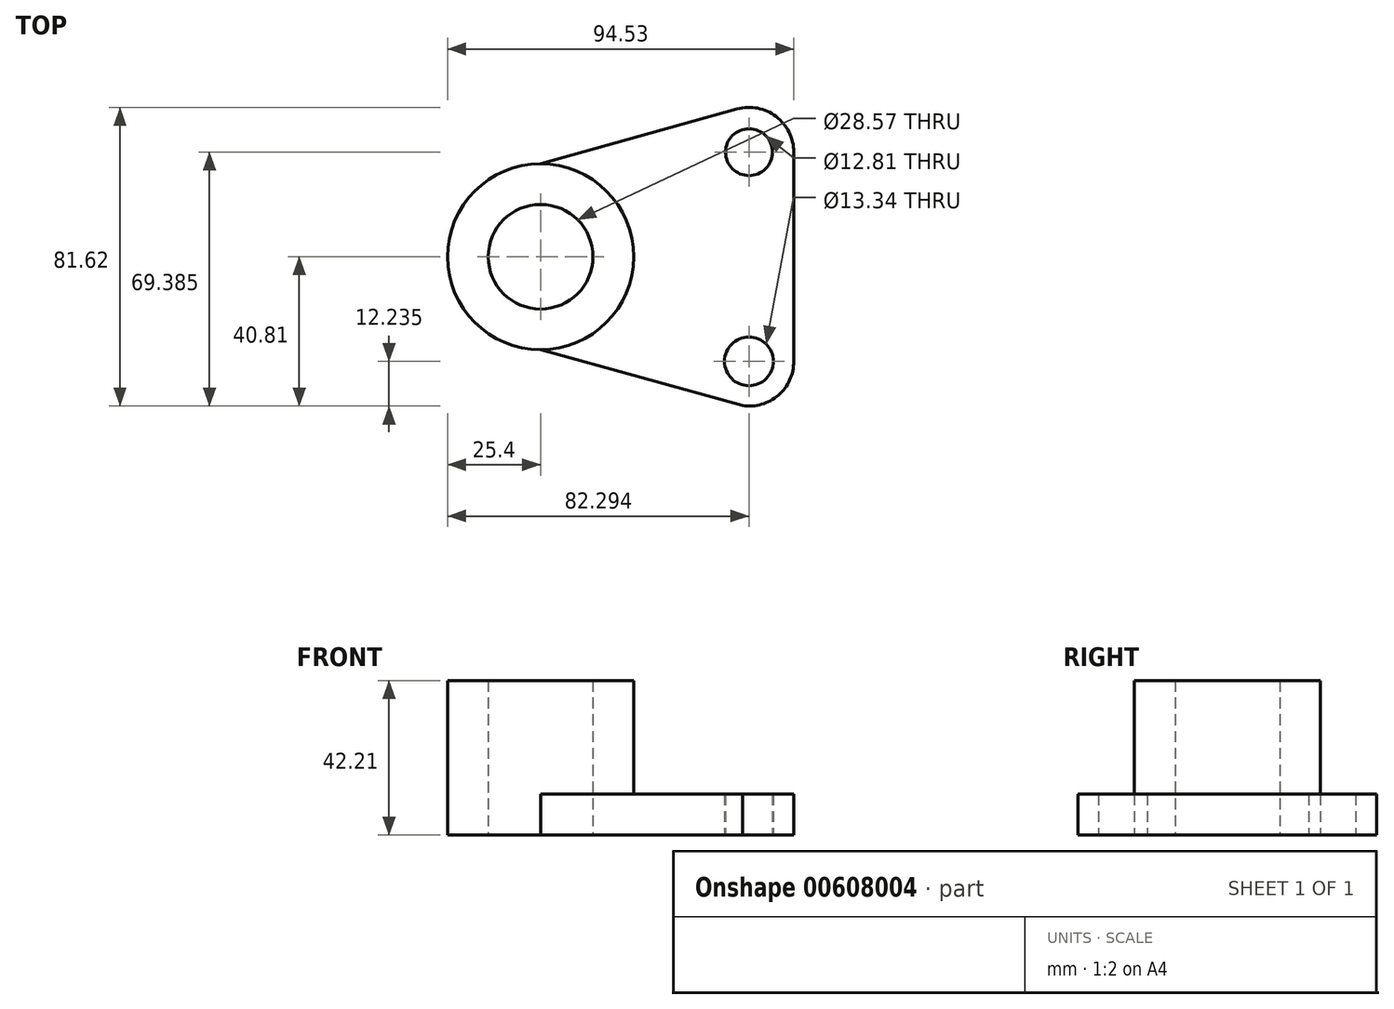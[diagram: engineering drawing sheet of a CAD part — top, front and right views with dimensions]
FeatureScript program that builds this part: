
annotation { "Feature Type Name" : "Feature", "Feature Type Description" : "" }
export const myFeature = defineFeature(function(context is Context, id is Id, definition is map)
    precondition{}
    {
        {
            var Q0;
            Q0=qCreatedBy(makeId("Top.planeOp"),FACE);
            var sketch = newSketch(context, id + "F0", { "sketchPlane" : qUnion([Q0])});
            skCircle(sketch, "E0", {"center": v(0, 0) * mm, "radius": 14.29 * mm});
            skCircle(sketch, "E1", {"center": v(0, 0) * mm, "radius": 25.4 * mm});
            skLineSegment(sketch, "E2", {"start": v(69.13, 28.58) * mm, "end": v(69.13, -28.58) * mm});
            skLineSegment(sketch, "E3", {"start": v(0, -25.4) * mm, "end": v(55.14, -40.68) * mm});
            skCircle(sketch, "E4", {"center": v(56.9, 28.58) * mm, "radius": 6.4 * mm});
            skCircle(sketch, "E5", {"center": v(56.9, -28.58) * mm, "radius": 6.67 * mm});
            skArc(sketch, "E6", {"start": v(55.14, -40.68) * mm, "mid": v(64.9, -37.82) * mm, "end": v(69.13, -28.58) * mm});
            skLineSegment(sketch, "E7", {"start": v(53.64, 40.37) * mm, "end": v(0, 25.4) * mm});
            skArc(sketch, "E8", {"start": v(69.13, 28.58) * mm, "mid": v(64.3, 38.3) * mm, "end": v(53.64, 40.37) * mm});
            skSolve(sketch);
        }
        {
            var Q0;
            Q0=makeQuery(id+"F0.imprint","IMPRINT",FACE,{"disambiguationData":[TD([[makeQuery(id+"F0.imprint","IMPRINT",EDGE,{"derivedFrom":sQuery(id+"F0.wireOp",EDGE,"E0")}),-1.0]])]});
            extrude(context, id + "F1", {"entities" : qUnion([Q0]), "depth" : 42.2 * mm, "offsetDistance" : 25.4 * mm});
        }
        {
            var Q0;
            Q0=makeQuery(id+"F0.imprint","IMPRINT",FACE,{"disambiguationData":[TD([[makeQuery(id+"F0.imprint","IMPRINT",EDGE,{"derivedFrom":sQuery(id+"F0.wireOp",EDGE,"E2")}),-1.0]])]});
            extrude(context, id + "F2", {"entities" : qUnion([Q0]), "operationType" : NewBodyOperationType.ADD, "depth" : 11.18 * mm, "offsetDistance" : 25.4 * mm});
        }
    });
